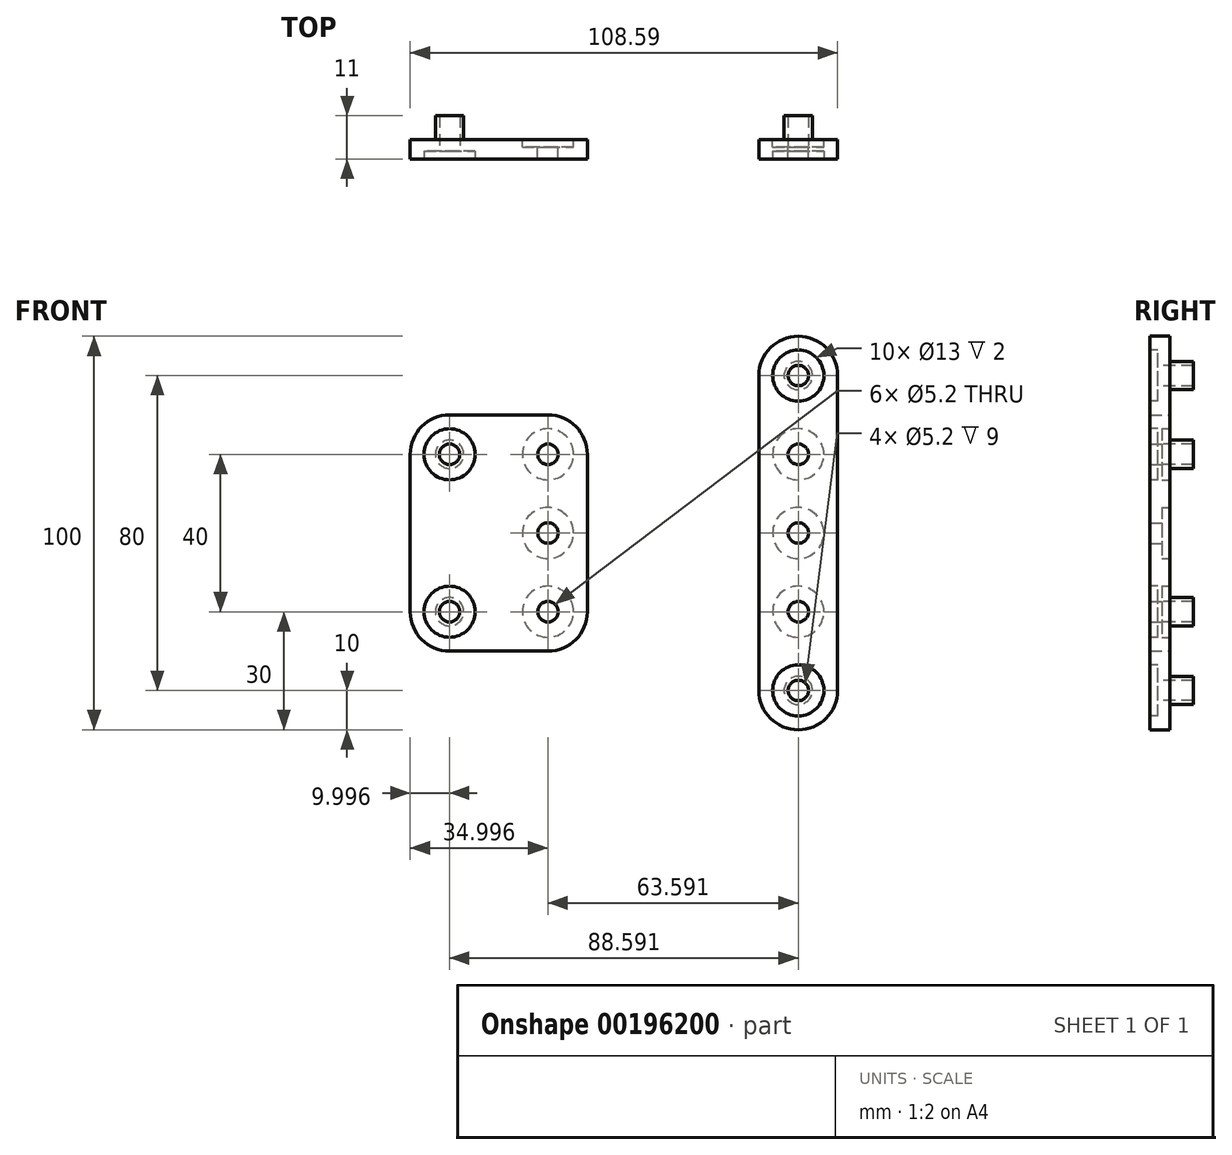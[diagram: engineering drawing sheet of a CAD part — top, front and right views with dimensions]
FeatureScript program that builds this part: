
annotation { "Feature Type Name" : "Feature", "Feature Type Description" : "" }
export const myFeature = defineFeature(function(context is Context, id is Id, definition is map)
    precondition{}
    {
        {
            var Q0;
            Q0=qCreatedBy(makeId("Front.planeOp"),FACE);
            var sketch = newSketch(context, id + "F0", { "sketchPlane" : qUnion([Q0])});
            skPoint(sketch, "E0", {"position": v(41.23, 20) * mm});
            skPoint(sketch, "E1", {"position": v(41.23, -20) * mm});
            skPoint(sketch, "E2", {"position": v(41.23, -40) * mm});
            skPoint(sketch, "E3", {"position": v(41.23, 40) * mm});
            skLineSegment(sketch, "E4.bottom", {"start": v(51.23, 50) * mm, "end": v(31.23, 50) * mm});
            skLineSegment(sketch, "E5", {"start": v(31.23, 50) * mm, "end": v(31.23, -50) * mm});
            skLineSegment(sketch, "E6", {"start": v(51.23, 50) * mm, "end": v(51.23, -50) * mm});
            skLineSegment(sketch, "E7", {"start": v(31.23, -50) * mm, "end": v(51.23, -50) * mm});
            skLineSegment(sketch, "E8", {"start": v(41.23, 40) * mm, "end": v(41.23, -40) * mm, "construction": true});
            skPoint(sketch, "E9", {"position": v(41.23, 0) * mm});
            skLineSegment(sketch, "E10", {"start": v(-22.36, 20) * mm, "end": v(-22.36, -20) * mm, "construction": true});
            skPoint(sketch, "E11", {"position": v(-22.36, 20) * mm});
            skPoint(sketch, "E12", {"position": v(-22.36, -20) * mm});
            skPoint(sketch, "E13", {"position": v(-22.36, 0) * mm});
            skLineSegment(sketch, "E14", {"start": v(-47.36, 20) * mm, "end": v(-47.36, -20) * mm, "construction": true});
            skLineSegment(sketch, "E15.bottom", {"start": v(-57.36, 30) * mm, "end": v(-12.36, 30) * mm});
            skLineSegment(sketch, "E15.top", {"start": v(-57.36, -30) * mm, "end": v(-12.36, -30) * mm});
            skLineSegment(sketch, "E15.left", {"start": v(-57.36, 30) * mm, "end": v(-57.36, -30) * mm});
            skLineSegment(sketch, "E15.right", {"start": v(-12.36, 30) * mm, "end": v(-12.36, -30) * mm});
            skCircle(sketch, "E16", {"center": v(-47.36, 20) * mm, "radius": 3.6 * mm});
            skCircle(sketch, "E17", {"center": v(-47.36, -20) * mm, "radius": 3.6 * mm});
            skCircle(sketch, "E18", {"center": v(41.23, 40) * mm, "radius": 3.6 * mm});
            skCircle(sketch, "E19", {"center": v(41.23, -40) * mm, "radius": 3.6 * mm});
            skSolve(sketch);
        }
        {
            var Q0;
            Q0=makeQuery(id+"F0.imprint","IMPRINT",FACE,{"disambiguationData":[TD([[makeQuery(id+"F0.imprint","IMPRINT",EDGE,{"derivedFrom":sQuery(id+"F0.wireOp",EDGE,"E4.bottom")}),1.0]])]});
            var Q1;
            Q1=makeQuery(id+"F0.imprint","IMPRINT",FACE,{"disambiguationData":[TD([[makeQuery(id+"F0.imprint","IMPRINT",EDGE,{"derivedFrom":sQuery(id+"F0.wireOp",EDGE,"E15.bottom")}),-1.0]])]});
            var Q2;
            Q2=makeQuery(id+"F0.imprint","IMPRINT",FACE,{"disambiguationData":[TD([[makeQuery(id+"F0.imprint","IMPRINT",EDGE,{"derivedFrom":sQuery(id+"F0.wireOp",EDGE,"E16")}),1.0]])]});
            var Q3;
            Q3=makeQuery(id+"F0.imprint","IMPRINT",FACE,{"disambiguationData":[TD([[makeQuery(id+"F0.imprint","IMPRINT",EDGE,{"derivedFrom":sQuery(id+"F0.wireOp",EDGE,"E17")}),1.0]])]});
            var Q4;
            Q4=makeQuery(id+"F0.imprint","IMPRINT",FACE,{"disambiguationData":[TD([[makeQuery(id+"F0.imprint","IMPRINT",EDGE,{"derivedFrom":sQuery(id+"F0.wireOp",EDGE,"E19")}),1.0]])]});
            var Q5;
            Q5=makeQuery(id+"F0.imprint","IMPRINT",FACE,{"disambiguationData":[TD([[makeQuery(id+"F0.imprint","IMPRINT",EDGE,{"derivedFrom":sQuery(id+"F0.wireOp",EDGE,"E18")}),1.0]])]});
            extrude(context, id + "F1", {"entities" : qUnion([Q0, Q1, Q2, Q3, Q4, Q5]), "depth" : 5 * mm});
        }
        {
            var Q0;
            Q0=makeQuery(id+"F0.imprint","IMPRINT",FACE,{"disambiguationData":[TD([[makeQuery(id+"F0.imprint","IMPRINT",EDGE,{"derivedFrom":sQuery(id+"F0.wireOp",EDGE,"E16")}),1.0]])]});
            var Q1;
            Q1=makeQuery(id+"F0.imprint","IMPRINT",FACE,{"disambiguationData":[TD([[makeQuery(id+"F0.imprint","IMPRINT",EDGE,{"derivedFrom":sQuery(id+"F0.wireOp",EDGE,"E17")}),1.0]])]});
            var Q2;
            Q2=makeQuery(id+"F0.imprint","IMPRINT",FACE,{"disambiguationData":[TD([[makeQuery(id+"F0.imprint","IMPRINT",EDGE,{"derivedFrom":sQuery(id+"F0.wireOp",EDGE,"E18")}),1.0]])]});
            var Q3;
            Q3=makeQuery(id+"F0.imprint","IMPRINT",FACE,{"disambiguationData":[TD([[makeQuery(id+"F0.imprint","IMPRINT",EDGE,{"derivedFrom":sQuery(id+"F0.wireOp",EDGE,"E19")}),1.0]])]});
            extrude(context, id + "F2", {"entities" : qUnion([Q0, Q1, Q2, Q3]), "operationType" : NewBodyOperationType.ADD, "oppositeDirection" : true, "depth" : 6 * mm});
        }
        {
            var Q0;
            Q0=makeQuery(id+"F1.opExtrude","CAP_FACE",FACE,{"disambiguationData":[OSD([sQuery(id+"F0.wireOp",EDGE,"86937541-f3f4-4503-8a13-7677f3d5582c.bottom"),sQuery(id+"F0.wireOp",EDGE,"86937541-f3f4-4503-8a13-7677f3d5582c.top"),sQuery(id+"F0.wireOp",EDGE,"86937541-f3f4-4503-8a13-7677f3d5582c.left"),sQuery(id+"F0.wireOp",EDGE,"E4.bottom"),sQuery(id+"F0.wireOp",EDGE,"E4.top"),sQuery(id+"F0.wireOp",EDGE,"E4.left"),sQuery(id+"F0.wireOp",EDGE,"E4.right"),sQuery(id+"F0.wireOp",EDGE,"a02ba8a6-a8d0-453a-8d98-62350bf48d8b.trimOffspring")])],"isStart":false});
            var sketch = newSketch(context, id + "F3", { "sketchPlane" : qUnion([Q0])});
            skLineSegment(sketch, "E20.0", {"start": v(41.23, 40) * mm, "end": v(41.23, -40) * mm, "construction": true});
            skPoint(sketch, "E21", {"position": v(41.23, 40) * mm});
            skPoint(sketch, "E22", {"position": v(41.23, -40) * mm});
            skLineSegment(sketch, "E23.0", {"start": v(-47.36, 20) * mm, "end": v(-47.36, -20) * mm, "construction": true});
            skPoint(sketch, "E24", {"position": v(-47.36, 20) * mm});
            skPoint(sketch, "E25", {"position": v(-47.36, -20) * mm});
            skSolve(sketch);
        }
        {
            var Q0;
            Q0=sQuery(id+"F0.wireOp",VERTEX,"E0");
            var Q1;
            Q1=sQuery(id+"F0.wireOp",VERTEX,"E9");
            var Q2;
            Q2=sQuery(id+"F0.wireOp",VERTEX,"E1");
            var Q3;
            Q3=sQuery(id+"F0.wireOp",VERTEX,"E11");
            var Q4;
            Q4=sQuery(id+"F0.wireOp",VERTEX,"E13");
            var Q5;
            Q5=sQuery(id+"F0.wireOp",VERTEX,"E12");
            var Q6;
            Q6=makeQuery(id+"F1.opExtrude","SWEPT_BODY",BODY,{"disambiguationData":[OSD([sQuery(id+"F0.wireOp",EDGE,"86937541-f3f4-4503-8a13-7677f3d5582c.bottom"),sQuery(id+"F0.wireOp",EDGE,"86937541-f3f4-4503-8a13-7677f3d5582c.top"),sQuery(id+"F0.wireOp",EDGE,"86937541-f3f4-4503-8a13-7677f3d5582c.left"),sQuery(id+"F0.wireOp",EDGE,"E4.bottom"),sQuery(id+"F0.wireOp",EDGE,"E4.top"),sQuery(id+"F0.wireOp",EDGE,"E4.left"),sQuery(id+"F0.wireOp",EDGE,"E4.right"),sQuery(id+"F0.wireOp",EDGE,"a02ba8a6-a8d0-453a-8d98-62350bf48d8b.trimOffspring")])]});
            var Q7;
            Q7=makeQuery(id+"F1.opExtrude","SWEPT_BODY",BODY,{"disambiguationData":[OSD([sQuery(id+"F0.wireOp",EDGE,"E15.bottom"),sQuery(id+"F0.wireOp",EDGE,"E15.top"),sQuery(id+"F0.wireOp",EDGE,"E15.left"),sQuery(id+"F0.wireOp",EDGE,"E15.right")])]});
            hole(context, id + "F4", {"style" : HoleStyle.C_BORE, "endStyle" : HoleEndStyle.THROUGH, "oppositeDirection" : true, "holeDiameter" : 5.2 * mm, "cBoreDiameter" : 13 * mm, "cBoreDepth" : 2 * mm, "locations" : qUnion([Q0, Q1, Q2, Q3, Q4, Q5]), "scope" : qUnion([Q6, Q7]), "isTappedThrough" : true});
        }
        {
            var Q0;
            Q0=makeQuery(id+"F1.opExtrude","SWEPT_EDGE",EDGE,{"disambiguationData":[OSD([sQuery(id+"F0.wireOp",EDGE,"E4.bottom"),sQuery(id+"F0.wireOp",EDGE,"E5")])]});
            var Q1;
            Q1=makeQuery(id+"F1.opExtrude","SWEPT_EDGE",EDGE,{"disambiguationData":[OSD([sQuery(id+"F0.wireOp",EDGE,"E4.bottom"),sQuery(id+"F0.wireOp",EDGE,"E6")])]});
            var Q2;
            Q2=makeQuery(id+"F1.opExtrude","SWEPT_EDGE",EDGE,{"disambiguationData":[OSD([sQuery(id+"F0.wireOp",EDGE,"E5"),sQuery(id+"F0.wireOp",EDGE,"E7")])]});
            var Q3;
            Q3=makeQuery(id+"F1.opExtrude","SWEPT_EDGE",EDGE,{"disambiguationData":[OSD([sQuery(id+"F0.wireOp",EDGE,"E6"),sQuery(id+"F0.wireOp",EDGE,"E7")])]});
            var Q4;
            Q4=makeQuery(id+"F1.opExtrude","SWEPT_EDGE",EDGE,{"disambiguationData":[OSD([sQuery(id+"F0.wireOp",EDGE,"E15.bottom"),sQuery(id+"F0.wireOp",EDGE,"E15.left")])]});
            var Q5;
            Q5=makeQuery(id+"F1.opExtrude","SWEPT_EDGE",EDGE,{"disambiguationData":[OSD([sQuery(id+"F0.wireOp",EDGE,"E15.top"),sQuery(id+"F0.wireOp",EDGE,"E15.left")])]});
            var Q6;
            Q6=makeQuery(id+"F1.opExtrude","SWEPT_EDGE",EDGE,{"disambiguationData":[OSD([sQuery(id+"F0.wireOp",EDGE,"E15.top"),sQuery(id+"F0.wireOp",EDGE,"E15.right")])]});
            var Q7;
            Q7=makeQuery(id+"F1.opExtrude","SWEPT_EDGE",EDGE,{"disambiguationData":[OSD([sQuery(id+"F0.wireOp",EDGE,"E15.bottom"),sQuery(id+"F0.wireOp",EDGE,"E15.right")])]});
            fillet(context, id + "F5", {"entities" : qUnion([Q0, Q1, Q2, Q3, Q4, Q5, Q6, Q7]), "radius" : 10 * mm, "tangentPropagation" : true, "allowEdgeOverflow" : false});
        }
        {
            var Q0;
            Q0=sQuery(id+"F3.wireOp",VERTEX,"E21");
            var Q1;
            Q1=sQuery(id+"F3.wireOp",VERTEX,"E22");
            var Q2;
            Q2=sQuery(id+"F3.wireOp",VERTEX,"E24");
            var Q3;
            Q3=sQuery(id+"F3.wireOp",VERTEX,"E25");
            var Q4;
            Q4=makeQuery(id+"F1.opExtrude","SWEPT_BODY",BODY,{"disambiguationData":[OSD([sQuery(id+"F0.wireOp",EDGE,"86937541-f3f4-4503-8a13-7677f3d5582c.bottom"),sQuery(id+"F0.wireOp",EDGE,"86937541-f3f4-4503-8a13-7677f3d5582c.top"),sQuery(id+"F0.wireOp",EDGE,"86937541-f3f4-4503-8a13-7677f3d5582c.left"),sQuery(id+"F0.wireOp",EDGE,"E4.bottom"),sQuery(id+"F0.wireOp",EDGE,"E4.top"),sQuery(id+"F0.wireOp",EDGE,"E4.left"),sQuery(id+"F0.wireOp",EDGE,"E4.right"),sQuery(id+"F0.wireOp",EDGE,"a02ba8a6-a8d0-453a-8d98-62350bf48d8b.trimOffspring")])]});
            var Q5;
            Q5=makeQuery(id+"F1.opExtrude","SWEPT_BODY",BODY,{"disambiguationData":[OSD([sQuery(id+"F0.wireOp",EDGE,"E15.bottom"),sQuery(id+"F0.wireOp",EDGE,"E15.top"),sQuery(id+"F0.wireOp",EDGE,"E15.left"),sQuery(id+"F0.wireOp",EDGE,"E15.right")])]});
            hole(context, id + "F6", {"style" : HoleStyle.C_BORE, "endStyle" : HoleEndStyle.THROUGH, "holeDiameter" : 5.2 * mm, "cBoreDiameter" : 13 * mm, "cBoreDepth" : 2 * mm, "locations" : qUnion([Q0, Q1, Q2, Q3]), "scope" : qUnion([Q4, Q5]), "isTappedThrough" : true});
        }
    });
